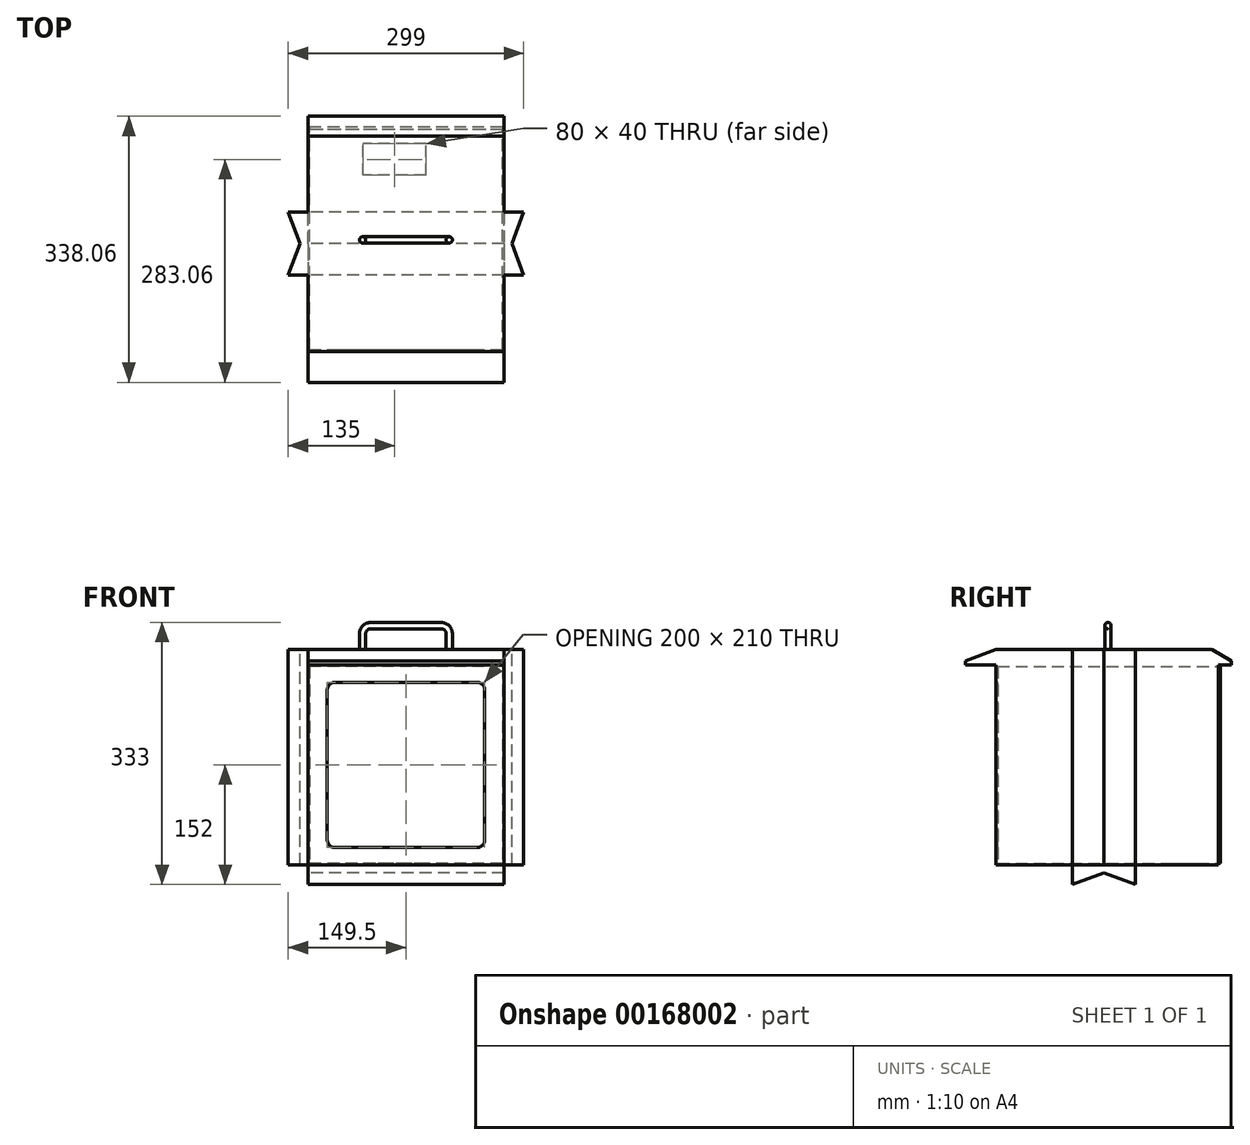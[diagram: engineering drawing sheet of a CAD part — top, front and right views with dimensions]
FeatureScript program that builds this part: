
annotation { "Feature Type Name" : "Feature", "Feature Type Description" : "" }
export const myFeature = defineFeature(function(context is Context, id is Id, definition is map)
    precondition{}
    {
        {
            var Q0;
            Q0=qCreatedBy(makeId("Front.planeOp"),FACE);
            var sketch = newSketch(context, id + "F0", { "sketchPlane" : qUnion([Q0])});
            skLineSegment(sketch, "E0.bottom", {"start": v(122.5, 125) * mm, "end": v(-122.5, 125) * mm});
            skLineSegment(sketch, "E0.top", {"start": v(122.5, -125) * mm, "end": v(-122.5, -125) * mm});
            skLineSegment(sketch, "E0.left", {"start": v(122.5, 125) * mm, "end": v(122.5, -125) * mm});
            skLineSegment(sketch, "E0.right", {"start": v(-122.5, 125) * mm, "end": v(-122.5, -125) * mm});
            skPoint(sketch, "E0.middle", {"position": v(0, 0) * mm});
            skLineSegment(sketch, "E1.0", {"start": v(124.5, 127) * mm, "end": v(-124.5, 127) * mm});
            skLineSegment(sketch, "E1.1", {"start": v(124.5, 127) * mm, "end": v(124.5, -127) * mm});
            skLineSegment(sketch, "E1.2", {"start": v(124.5, -127) * mm, "end": v(-124.5, -127) * mm});
            skLineSegment(sketch, "E1.3", {"start": v(-124.5, 127) * mm, "end": v(-124.5, -127) * mm});
            skSolve(sketch);
        }
        {
            var Q0;
            Q0=makeQuery(id+"F0.imprint","IMPRINT",FACE,{"disambiguationData":[TD([[makeQuery(id+"F0.imprint","IMPRINT",EDGE,{"derivedFrom":sQuery(id+"F0.wireOp",EDGE,"E0.bottom")}),-1.0]])]});
            extrude(context, id + "F1", {"entities" : qUnion([Q0]), "depth" : 280 * mm, "symmetric" : true});
        }
        {
            var Q0;
            Q0=makeQuery(id+"F1.opExtrude","CAP_FACE",FACE,{"disambiguationData":[OSD([sQuery(id+"F0.wireOp",EDGE,"E0.bottom"),sQuery(id+"F0.wireOp",EDGE,"E0.top"),sQuery(id+"F0.wireOp",EDGE,"E0.left"),sQuery(id+"F0.wireOp",EDGE,"E0.right"),sQuery(id+"F0.wireOp",EDGE,"E1.0"),sQuery(id+"F0.wireOp",EDGE,"E1.1"),sQuery(id+"F0.wireOp",EDGE,"E1.2"),sQuery(id+"F0.wireOp",EDGE,"E1.3")])],"isStart":false});
            var sketch = newSketch(context, id + "F2", { "sketchPlane" : qUnion([Q0])});
            skLineSegment(sketch, "E2.0", {"start": v(124.5, 127) * mm, "end": v(-124.5, 127) * mm});
            skLineSegment(sketch, "E3.0", {"start": v(-124.5, 127) * mm, "end": v(-124.5, -127) * mm});
            skLineSegment(sketch, "E4.0", {"start": v(124.5, 127) * mm, "end": v(124.5, -127) * mm});
            skLineSegment(sketch, "E5.0", {"start": v(124.5, -127) * mm, "end": v(-124.5, -127) * mm});
            skSolve(sketch);
        }
        {
            var Q0;
            Q0 = qSketchRegion(id + "F2", true);
            extrude(context, id + "F3", {"entities" : qUnion([Q0]), "operationType" : NewBodyOperationType.ADD, "depth" : 2 * mm});
        }
        {
            var Q0;
            Q0=makeQuery(id+"F1.opExtrude","CAP_FACE",FACE,{"disambiguationData":[OSD([sQuery(id+"F0.wireOp",EDGE,"E0.bottom"),sQuery(id+"F0.wireOp",EDGE,"E0.top"),sQuery(id+"F0.wireOp",EDGE,"E0.left"),sQuery(id+"F0.wireOp",EDGE,"E0.right"),sQuery(id+"F0.wireOp",EDGE,"E1.0"),sQuery(id+"F0.wireOp",EDGE,"E1.1"),sQuery(id+"F0.wireOp",EDGE,"E1.2"),sQuery(id+"F0.wireOp",EDGE,"E1.3")])],"isStart":true});
            var sketch = newSketch(context, id + "F4", { "sketchPlane" : qUnion([Q0])});
            skLineSegment(sketch, "E6.0", {"start": v(-124.5, 127) * mm, "end": v(124.5, 127) * mm});
            skLineSegment(sketch, "E7.0", {"start": v(-124.5, 127) * mm, "end": v(-124.5, -127) * mm});
            skLineSegment(sketch, "E8.0", {"start": v(124.5, 127) * mm, "end": v(124.5, -127) * mm});
            skLineSegment(sketch, "E9.0", {"start": v(-124.5, -127) * mm, "end": v(124.5, -127) * mm});
            skSolve(sketch);
        }
        {
            var Q0;
            Q0=makeQuery(id+"FptgfN2QlaSVx9k_1.boolean.opBoolean","MERGE",FACE,{"derivedFrom":[makeQuery(id+"F3.boolean.opBoolean","MERGE",FACE,{"derivedFrom":[makeQuery(id+"F1.opExtrude","SWEPT_FACE",FACE,{"disambiguationData":[OSD([sQuery(id+"F0.wireOp",EDGE,"E1.1")])]}),makeQuery(id+"F3.opExtrude","SWEPT_FACE",FACE,{"disambiguationData":[OSD([sQuery(id+"F2.wireOp",EDGE,"E4.0")])]})]}),makeQuery(id+"FptgfN2QlaSVx9k_1.opExtrude","SWEPT_FACE",FACE,{"disambiguationData":[OSD([sQuery(id+"F4.wireOp",EDGE,"E7.0")])]})]});
            var sketch = newSketch(context, id + "F5", { "sketchPlane" : qUnion([Q0])});
            skLineSegment(sketch, "E10.0", {"start": v(-142, 127) * mm, "end": v(132, 127) * mm});
            skLineSegment(sketch, "E11", {"start": v(-142, 127) * mm, "end": v(-181.06, 127) * mm});
            skLineSegment(sketch, "E12", {"start": v(132, 127) * mm, "end": v(132, 147) * mm});
            skLineSegment(sketch, "E13", {"start": v(132, 147) * mm, "end": v(-142, 147) * mm});
            skLineSegment(sketch, "E14", {"start": v(-142, 147) * mm, "end": v(-181.06, 132) * mm});
            skLineSegment(sketch, "E15", {"start": v(-181.06, 132) * mm, "end": v(-181.06, 127) * mm});
            skSolve(sketch);
        }
        {
            var Q0;
            Q0 = qSketchRegion(id + "F5", true);
            var Q1;
            Q1=makeQuery(id+"FptgfN2QlaSVx9k_1.boolean.opBoolean","MERGE",FACE,{"derivedFrom":[makeQuery(id+"F3.boolean.opBoolean","MERGE",FACE,{"derivedFrom":[makeQuery(id+"F1.opExtrude","SWEPT_FACE",FACE,{"disambiguationData":[OSD([sQuery(id+"F0.wireOp",EDGE,"E1.3")])]}),makeQuery(id+"F3.opExtrude","SWEPT_FACE",FACE,{"disambiguationData":[OSD([sQuery(id+"F2.wireOp",EDGE,"E3.0")])]})]}),makeQuery(id+"FptgfN2QlaSVx9k_1.opExtrude","SWEPT_FACE",FACE,{"disambiguationData":[OSD([sQuery(id+"F4.wireOp",EDGE,"E8.0")])]})]});
            extrude(context, id + "F6", {"entities" : qUnion([Q0]), "operationType" : NewBodyOperationType.ADD, "endBound" : BoundingType.UP_TO_SURFACE, "oppositeDirection" : true, "endBoundEntityFace" : qUnion([Q1]), "depth" : 209 * mm});
        }
        {
            var Q0;
            Q0=makeQuery(id+"F3.opExtrude","CAP_FACE",FACE,{"disambiguationData":[OSD([sQuery(id+"F2.wireOp",EDGE,"E2.0"),sQuery(id+"F2.wireOp",EDGE,"E3.0"),sQuery(id+"F2.wireOp",EDGE,"E4.0"),sQuery(id+"F2.wireOp",EDGE,"E5.0")])],"isStart":false});
            var sketch = newSketch(context, id + "F7", { "sketchPlane" : qUnion([Q0])});
            skPoint(sketch, "E16.middle", {"position": v(0, 0) * mm});
            skLineSegment(sketch, "E17.bottom", {"start": v(90, -105) * mm, "end": v(-90, -105) * mm});
            skLineSegment(sketch, "E17.top", {"start": v(90, 105) * mm, "end": v(-90, 105) * mm});
            skLineSegment(sketch, "E17.left", {"start": v(100, -95) * mm, "end": v(100, 95) * mm});
            skLineSegment(sketch, "E17.right", {"start": v(-100, -95) * mm, "end": v(-100, 95) * mm});
            skPoint(sketch, "E18.visualSharp", {"position": v(-100, 105) * mm});
            skArc(sketch, "E18.filletArc", {"start": v(-90, 105) * mm, "mid": v(-97.07, 102.07) * mm, "end": v(-100, 95) * mm});
            skPoint(sketch, "E19.visualSharp", {"position": v(100, 105) * mm});
            skArc(sketch, "E19.filletArc", {"start": v(100, 95) * mm, "mid": v(97.07, 102.07) * mm, "end": v(90, 105) * mm});
            skPoint(sketch, "E20.visualSharp", {"position": v(100, -105) * mm});
            skArc(sketch, "E20.filletArc", {"start": v(90, -105) * mm, "mid": v(97.07, -102.07) * mm, "end": v(100, -95) * mm});
            skPoint(sketch, "E21.visualSharp", {"position": v(-100, -105) * mm});
            skArc(sketch, "E21.filletArc", {"start": v(-100, -95) * mm, "mid": v(-97.07, -102.07) * mm, "end": v(-90, -105) * mm});
            skSolve(sketch);
        }
        {
            var Q0;
            Q0 = qSketchRegion(id + "F7", true);
            extrude(context, id + "F8", {"entities" : qUnion([Q0]), "operationType" : NewBodyOperationType.REMOVE, "oppositeDirection" : true, "depth" : 25 * mm});
        }
        {
            var Q0;
            Q0=makeQuery(id+"FptgfN2QlaSVx9k_1.boolean.opBoolean","MERGE",FACE,{"derivedFrom":[makeQuery(id+"F3.boolean.opBoolean","MERGE",FACE,{"derivedFrom":[makeQuery(id+"F1.opExtrude","SWEPT_FACE",FACE,{"disambiguationData":[OSD([sQuery(id+"F0.wireOp",EDGE,"E1.2")])]}),makeQuery(id+"F3.opExtrude","SWEPT_FACE",FACE,{"disambiguationData":[OSD([sQuery(id+"F2.wireOp",EDGE,"E5.0")])]})]}),makeQuery(id+"FptgfN2QlaSVx9k_1.opExtrude","SWEPT_FACE",FACE,{"disambiguationData":[OSD([sQuery(id+"F4.wireOp",EDGE,"E9.0")])]})]});
            var sketch = newSketch(context, id + "F9", { "sketchPlane" : qUnion([Q0])});
            skPoint(sketch, "E22.centerSnap0", {"position": v(-124.5, 1) * mm});
            skLineSegment(sketch, "E23.0", {"start": v(124.5, 142) * mm, "end": v(124.5, -142) * mm});
            skLineSegment(sketch, "E24.0", {"start": v(-124.5, 142) * mm, "end": v(-124.5, -142) * mm});
            skLineSegment(sketch, "E25.bottom", {"start": v(25.5, -82) * mm, "end": v(-54.5, -82) * mm});
            skLineSegment(sketch, "E25.top", {"start": v(25.5, -122) * mm, "end": v(-54.5, -122) * mm});
            skLineSegment(sketch, "E25.left", {"start": v(25.5, -82) * mm, "end": v(25.5, -122) * mm});
            skLineSegment(sketch, "E25.right", {"start": v(-54.5, -82) * mm, "end": v(-54.5, -122) * mm});
            skPoint(sketch, "E25.middle", {"position": v(0, -102) * mm});
            skSolve(sketch);
        }
        {
            var Q0;
            Q0 = qSketchRegion(id + "F9", true);
            extrude(context, id + "F10", {"entities" : qUnion([Q0]), "operationType" : NewBodyOperationType.REMOVE, "oppositeDirection" : true, "depth" : 25 * mm});
        }
        {
            var Q0;
            Q0=makeQuery(id+"F6.opExtrude","SWEPT_FACE",FACE,{"disambiguationData":[OSD([sQuery(id+"F5.wireOp",EDGE,"E13")])]});
            var sketch = newSketch(context, id + "F11", { "sketchPlane" : qUnion([Q0])});
            skCircle(sketch, "E26", {"center": v(-55, 0) * mm, "radius": 4 * mm});
            skCircle(sketch, "E27.MirrorC", {"center": v(55, 0) * mm, "radius": 4 * mm});
            skSolve(sketch);
        }
        {
            var Q0;
            Q0=qCreatedBy(makeId("Front.planeOp"),FACE);
            var sketch = newSketch(context, id + "F12", { "sketchPlane" : qUnion([Q0])});
            skPoint(sketch, "E28.0", {"position": v(-55, 147) * mm});
            skPoint(sketch, "E29.0", {"position": v(55, 147) * mm});
            skLineSegment(sketch, "E30", {"start": v(-55, 147) * mm, "end": v(-55, 167) * mm});
            skLineSegment(sketch, "E31", {"start": v(-45, 177) * mm, "end": v(45, 177) * mm});
            skLineSegment(sketch, "E32", {"start": v(55, 167) * mm, "end": v(55, 147) * mm});
            skPoint(sketch, "E33.visualSharp", {"position": v(-55, 177) * mm});
            skArc(sketch, "E33.filletArc", {"start": v(-45, 177) * mm, "mid": v(-52.07, 174.07) * mm, "end": v(-55, 167) * mm});
            skPoint(sketch, "E34.visualSharp", {"position": v(55, 177) * mm});
            skArc(sketch, "E34.filletArc", {"start": v(55, 167) * mm, "mid": v(52.07, 174.07) * mm, "end": v(45, 177) * mm});
            skSolve(sketch);
        }
        {
            var Q0;
            Q0=makeQuery(id+"F11.imprint","IMPRINT",FACE,{"disambiguationData":[TD([[makeQuery(id+"F11.imprint","IMPRINT",EDGE,{"derivedFrom":sQuery(id+"F11.wireOp",EDGE,"E26")}),1.0]])]});
            var Q1;
            Q1 = qConstructionFilter(qBodyType(qCreatedBy(id + "F12" ,EDGE), BodyType.WIRE), ConstructionObject.NO);
            sweep(context, id + "F13", {"operationType" : NewBodyOperationType.ADD, "profiles" : qUnion([Q0]), "path" : qUnion([Q1])});
        }
        {
            var Q0;
            Q0=makeQuery(id+"F6.opExtrude","SWEPT_FACE",FACE,{"disambiguationData":[OSD([sQuery(id+"F5.wireOp",EDGE,"E13")])]});
            var sketch = newSketch(context, id + "F14", { "sketchPlane" : qUnion([Q0])});
            skLineSegment(sketch, "E35.0", {"start": v(-124.5, -142) * mm, "end": v(-124.5, 132) * mm});
            skLineSegment(sketch, "E36.0", {"start": v(124.5, 132) * mm, "end": v(124.5, -142) * mm});
            skLineSegment(sketch, "E37.bottom", {"start": v(-124.5, -45) * mm, "end": v(-124.5, -45) * mm});
            skLineSegment(sketch, "E37.top", {"start": v(-124.5, 35) * mm, "end": v(-124.5, 35) * mm});
            skLineSegment(sketch, "E37.left", {"start": v(-124.5, -45) * mm, "end": v(-124.5, 35) * mm});
            skLineSegment(sketch, "E37.right", {"start": v(-124.5, -45) * mm, "end": v(-124.5, 35) * mm});
            skPoint(sketch, "E37.middle", {"position": v(-124.5, -5) * mm});
            skLineSegment(sketch, "E38", {"start": v(-124.5, 35) * mm, "end": v(-149.5, 35) * mm});
            skLineSegment(sketch, "E39", {"start": v(-149.5, -45) * mm, "end": v(-124.5, -45) * mm});
            skLineSegment(sketch, "E40", {"start": v(-134.5, -5) * mm, "end": v(-149.5, 35) * mm});
            skLineSegment(sketch, "E41", {"start": v(-134.5, -5) * mm, "end": v(-149.5, -45) * mm});
            skLineSegment(sketch, "E42.MirrorCS", {"start": v(124.5, -45) * mm, "end": v(124.5, 35) * mm});
            skLineSegment(sketch, "E43.MirrorCS", {"start": v(149.5, -45) * mm, "end": v(124.5, -45) * mm});
            skLineSegment(sketch, "E44.MirrorCS", {"start": v(134.5, -5) * mm, "end": v(149.5, -45) * mm});
            skLineSegment(sketch, "E45.MirrorCS", {"start": v(134.5, -5) * mm, "end": v(149.5, 35) * mm});
            skLineSegment(sketch, "E46.MirrorCS", {"start": v(124.5, 35) * mm, "end": v(149.5, 35) * mm});
            skSolve(sketch);
        }
        {
            var Q0;
            Q0 = qSketchRegion(id + "F14", true);
            var Q1;
            Q1=makeQuery(id+"FptgfN2QlaSVx9k_1.boolean.opBoolean","MERGE",FACE,{"derivedFrom":[makeQuery(id+"F3.boolean.opBoolean","MERGE",FACE,{"derivedFrom":[makeQuery(id+"F1.opExtrude","SWEPT_FACE",FACE,{"disambiguationData":[OSD([sQuery(id+"F0.wireOp",EDGE,"E1.2")])]}),makeQuery(id+"F3.opExtrude","SWEPT_FACE",FACE,{"disambiguationData":[OSD([sQuery(id+"F2.wireOp",EDGE,"E5.0")])]})]}),makeQuery(id+"FptgfN2QlaSVx9k_1.opExtrude","SWEPT_FACE",FACE,{"disambiguationData":[OSD([sQuery(id+"F4.wireOp",EDGE,"E9.0")])]})]});
            extrude(context, id + "F15", {"entities" : qUnion([Q0]), "operationType" : NewBodyOperationType.ADD, "endBound" : BoundingType.UP_TO_SURFACE, "oppositeDirection" : true, "endBoundEntityFace" : qUnion([Q1]), "depth" : 25 * mm});
        }
        {
            var Q0;
            {var subQ13=sQuery(id+"F4.wireOp",EDGE,"E8.0");var subQ14=sQuery(id+"F2.wireOp",EDGE,"E3.0");var subQ15=sQuery(id+"F0.wireOp",EDGE,"E1.3");Q0=makeQuery(id+"F15.boolean.opBoolean","SPLIT",FACE,{"disambiguationData":[TD([makeQuery(id+"F6.opExtrude","SWEPT_FACE",FACE,{"disambiguationData":[OSD([sQuery(id+"F5.wireOp",EDGE,"E12")])]})])],"derivedFrom":makeQuery(id+"F6.boolean.opBoolean","MERGE",FACE,{"derivedFrom":[makeQuery(id+"FptgfN2QlaSVx9k_1.boolean.opBoolean","MERGE",FACE,{"derivedFrom":[makeQuery(id+"F3.boolean.opBoolean","MERGE",FACE,{"derivedFrom":[makeQuery(id+"F1.opExtrude","SWEPT_FACE",FACE,{"disambiguationData":[OSD([subQ15])]}),makeQuery(id+"F3.opExtrude","SWEPT_FACE",FACE,{"disambiguationData":[OSD([subQ14])]})]}),makeQuery(id+"FptgfN2QlaSVx9k_1.opExtrude","SWEPT_FACE",FACE,{"disambiguationData":[OSD([subQ13])]})]}),makeQuery(id+"F6.opExtrude","CAP_FACE",FACE,{"disambiguationData":[OSD([subQ15,subQ14,subQ13])],"isStart":false})]})});}
            var sketch = newSketch(context, id + "F16", { "sketchPlane" : qUnion([Q0])});
            skLineSegment(sketch, "E47.bottom", {"start": v(-35, -127) * mm, "end": v(45, -127) * mm});
            skLineSegment(sketch, "E47.left", {"start": v(-35, -127) * mm, "end": v(-35, -152) * mm});
            skLineSegment(sketch, "E47.right", {"start": v(45, -127) * mm, "end": v(45, -152) * mm});
            skPoint(sketch, "E48.endSnap0", {"position": v(5, -127) * mm});
            skLineSegment(sketch, "E49", {"start": v(5, -137) * mm, "end": v(-35, -152) * mm});
            skLineSegment(sketch, "E50", {"start": v(5, -137) * mm, "end": v(45, -152) * mm});
            skPoint(sketch, "E48.start.orphan", {"position": v(5, -127) * mm});
            skSolve(sketch);
        }
        {
            var Q0;
            Q0 = qSketchRegion(id + "F16", true);
            var Q1;
            {var subQ13=sQuery(id+"F5.wireOp",EDGE,"E13");var subQ14=sQuery(id+"F5.wireOp",EDGE,"E12");var subQ15=sQuery(id+"F4.wireOp",EDGE,"E7.0");Q1=makeQuery(id+"F15.boolean.opBoolean","SPLIT",FACE,{"disambiguationData":[TD([makeQuery(id+"F6.opExtrude","SWEPT_FACE",FACE,{"disambiguationData":[OSD([subQ14])]})])],"derivedFrom":makeQuery(id+"F6.boolean.opBoolean","MERGE",FACE,{"derivedFrom":[makeQuery(id+"FptgfN2QlaSVx9k_1.boolean.opBoolean","MERGE",FACE,{"derivedFrom":[makeQuery(id+"F3.boolean.opBoolean","MERGE",FACE,{"derivedFrom":[makeQuery(id+"F1.opExtrude","SWEPT_FACE",FACE,{"disambiguationData":[OSD([sQuery(id+"F0.wireOp",EDGE,"E1.1")])]}),makeQuery(id+"F3.opExtrude","SWEPT_FACE",FACE,{"disambiguationData":[OSD([sQuery(id+"F2.wireOp",EDGE,"E4.0")])]})]}),makeQuery(id+"FptgfN2QlaSVx9k_1.opExtrude","SWEPT_FACE",FACE,{"disambiguationData":[OSD([subQ15])]})]}),makeQuery(id+"F6.opExtrude","CAP_FACE",FACE,{"disambiguationData":[OSD([sQuery(id+"F5.wireOp",EDGE,"E10.0"),sQuery(id+"F5.wireOp",EDGE,"E11"),subQ14,subQ13,sQuery(id+"F5.wireOp",EDGE,"E14"),sQuery(id+"F5.wireOp",EDGE,"E15")])],"isStart":true})]})});}
            extrude(context, id + "F17", {"entities" : qUnion([Q0]), "operationType" : NewBodyOperationType.ADD, "endBound" : BoundingType.UP_TO_SURFACE, "oppositeDirection" : true, "endBoundEntityFace" : qUnion([Q1]), "depth" : 25 * mm});
        }
        {
            var Q0;
            {var subQ13=sQuery(id+"F5.wireOp",EDGE,"E13");var subQ14=sQuery(id+"F5.wireOp",EDGE,"E12");var subQ15=sQuery(id+"F4.wireOp",EDGE,"E7.0");Q0=makeQuery(id+"F15.boolean.opBoolean","SPLIT",FACE,{"disambiguationData":[TD([makeQuery(id+"F6.opExtrude","SWEPT_FACE",FACE,{"disambiguationData":[OSD([subQ14])]})])],"derivedFrom":makeQuery(id+"F6.boolean.opBoolean","MERGE",FACE,{"derivedFrom":[makeQuery(id+"FptgfN2QlaSVx9k_1.boolean.opBoolean","MERGE",FACE,{"derivedFrom":[makeQuery(id+"F3.boolean.opBoolean","MERGE",FACE,{"derivedFrom":[makeQuery(id+"F1.opExtrude","SWEPT_FACE",FACE,{"disambiguationData":[OSD([sQuery(id+"F0.wireOp",EDGE,"E1.1")])]}),makeQuery(id+"F3.opExtrude","SWEPT_FACE",FACE,{"disambiguationData":[OSD([sQuery(id+"F2.wireOp",EDGE,"E4.0")])]})]}),makeQuery(id+"FptgfN2QlaSVx9k_1.opExtrude","SWEPT_FACE",FACE,{"disambiguationData":[OSD([subQ15])]})]}),makeQuery(id+"F6.opExtrude","CAP_FACE",FACE,{"disambiguationData":[OSD([sQuery(id+"F5.wireOp",EDGE,"E10.0"),sQuery(id+"F5.wireOp",EDGE,"E11"),subQ14,subQ13,sQuery(id+"F5.wireOp",EDGE,"E14"),sQuery(id+"F5.wireOp",EDGE,"E15")])],"isStart":true})]})});}
            var sketch = newSketch(context, id + "F18", { "sketchPlane" : qUnion([Q0])});
            skPoint(sketch, "E51.0", {"position": v(-142, 127) * mm});
            skLineSegment(sketch, "E52", {"start": v(132, 127) * mm, "end": v(157, 127) * mm});
            skLineSegment(sketch, "E53", {"start": v(157, 127) * mm, "end": v(157, 132) * mm});
            skLineSegment(sketch, "E54", {"start": v(157, 132) * mm, "end": v(132, 147) * mm});
            skSolve(sketch);
        }
        {
            var Q0;
            {var subQ0=sQuery(id+"F18.wireOp",EDGE,"E52");Q0=makeQuery(id+"F18.imprint","IMPRINT",FACE,{"disambiguationData":[TD([[makeQuery(id+"F18.imprint","IMPRINT",EDGE,{"derivedFrom":subQ0}),1.0]])]});}
            var Q1;
            {var subQ13=sQuery(id+"F4.wireOp",EDGE,"E8.0");var subQ14=sQuery(id+"F2.wireOp",EDGE,"E3.0");var subQ15=sQuery(id+"F0.wireOp",EDGE,"E1.3");Q1=makeQuery(id+"F15.boolean.opBoolean","SPLIT",FACE,{"disambiguationData":[TD([makeQuery(id+"F6.opExtrude","SWEPT_FACE",FACE,{"disambiguationData":[OSD([sQuery(id+"F5.wireOp",EDGE,"E12")])]})])],"derivedFrom":makeQuery(id+"F6.boolean.opBoolean","MERGE",FACE,{"derivedFrom":[makeQuery(id+"FptgfN2QlaSVx9k_1.boolean.opBoolean","MERGE",FACE,{"derivedFrom":[makeQuery(id+"F3.boolean.opBoolean","MERGE",FACE,{"derivedFrom":[makeQuery(id+"F1.opExtrude","SWEPT_FACE",FACE,{"disambiguationData":[OSD([subQ15])]}),makeQuery(id+"F3.opExtrude","SWEPT_FACE",FACE,{"disambiguationData":[OSD([subQ14])]})]}),makeQuery(id+"FptgfN2QlaSVx9k_1.opExtrude","SWEPT_FACE",FACE,{"disambiguationData":[OSD([subQ13])]})]}),makeQuery(id+"F6.opExtrude","CAP_FACE",FACE,{"disambiguationData":[OSD([subQ15,subQ14,subQ13])],"isStart":false})]})});}
            extrude(context, id + "F19", {"entities" : qUnion([Q0]), "operationType" : NewBodyOperationType.ADD, "endBound" : BoundingType.UP_TO_SURFACE, "oppositeDirection" : true, "endBoundEntityFace" : qUnion([Q1]), "depth" : 25 * mm});
        }
        {
            var Q0;
            Q0=makeQuery(id+"F4.imprint","IMPRINT",FACE,{"disambiguationData":[TD([[makeQuery(id+"F4.imprint","IMPRINT",EDGE,{"derivedFrom":makeQuery(id+"F1.opExtrude","CAP_EDGE",EDGE,{"disambiguationData":[OSD([sQuery(id+"F0.wireOp",EDGE,"E0.bottom")])],"isStart":true})}),-1.0]])]});
            var sketch = newSketch(context, id + "F20", { "sketchPlane" : qUnion([Q0])});
            skLineSegment(sketch, "E55.0.0", {"start": v(122.5, 125) * mm, "end": v(-122.5, 125) * mm});
            skLineSegment(sketch, "E55.0.1", {"start": v(-122.5, 125) * mm, "end": v(-122.5, -125) * mm});
            skLineSegment(sketch, "E55.0.2", {"start": v(-122.5, -125) * mm, "end": v(122.5, -125) * mm});
            skLineSegment(sketch, "E55.0.3", {"start": v(122.5, -125) * mm, "end": v(122.5, 125) * mm});
            skSolve(sketch);
        }
        {
            var Q0;
            Q0 = qSketchRegion(id + "F20", true);
            extrude(context, id + "F21", {"entities" : qUnion([Q0]), "depth" : 3 * mm, "offsetDistance" : 25 * mm});
        }
    });
